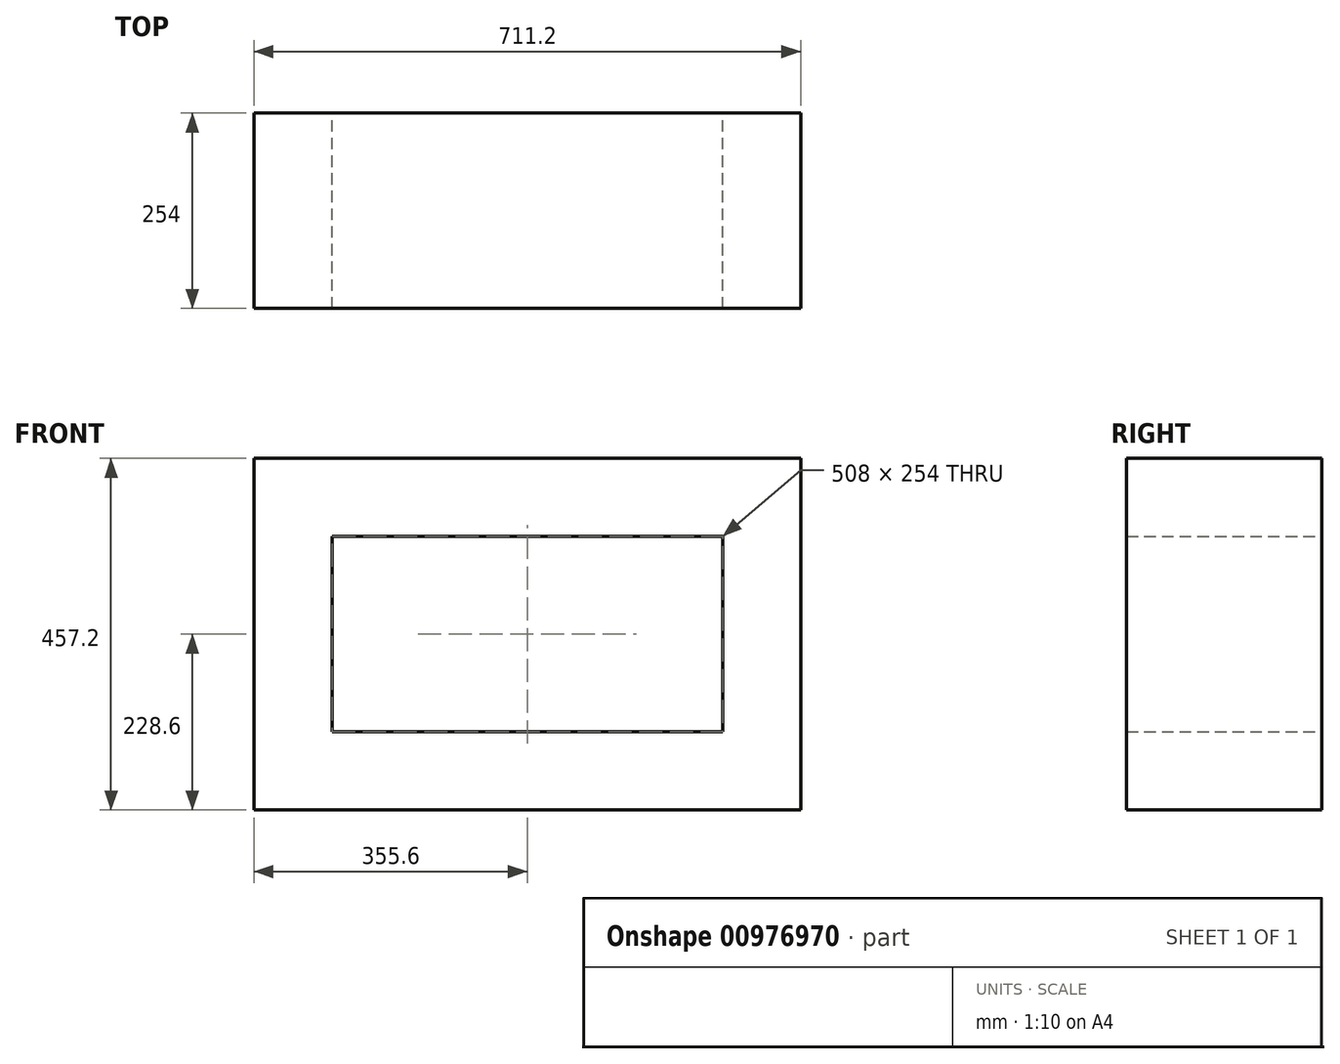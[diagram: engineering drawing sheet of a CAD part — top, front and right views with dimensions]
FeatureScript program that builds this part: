
annotation { "Feature Type Name" : "Feature", "Feature Type Description" : "" }
export const myFeature = defineFeature(function(context is Context, id is Id, definition is map)
    precondition{}
    {
        {
            var Q0;
            Q0=qCreatedBy(makeId("Front.planeOp"),FACE);
            var sketch = newSketch(context, id + "F0", { "sketchPlane" : qUnion([Q0])});
            skLineSegment(sketch, "E0.bottom", {"start": v(254, 127) * mm, "end": v(-254, 127) * mm});
            skLineSegment(sketch, "E0.top", {"start": v(254, -127) * mm, "end": v(-254, -127) * mm});
            skLineSegment(sketch, "E0.left", {"start": v(254, 127) * mm, "end": v(254, -127) * mm});
            skLineSegment(sketch, "E0.right", {"start": v(-254, 127) * mm, "end": v(-254, -127) * mm});
            skPoint(sketch, "E0.middle", {"position": v(0, 0) * mm});
            skLineSegment(sketch, "E1.0", {"start": v(355.6, 228.6) * mm, "end": v(-355.6, 228.6) * mm});
            skLineSegment(sketch, "E1.1", {"start": v(355.6, 228.6) * mm, "end": v(355.6, -228.6) * mm});
            skLineSegment(sketch, "E1.2", {"start": v(355.6, -228.6) * mm, "end": v(-355.6, -228.6) * mm});
            skLineSegment(sketch, "E1.3", {"start": v(-355.6, 228.6) * mm, "end": v(-355.6, -228.6) * mm});
            skSolve(sketch);
        }
        {
            var Q0;
            Q0 = qSketchRegion(id + "F0", true);
            extrude(context, id + "F1", {"entities" : qUnion([Q0]), "depth" : 254 * mm, "offsetDistance" : 25.4 * mm});
        }
    });
